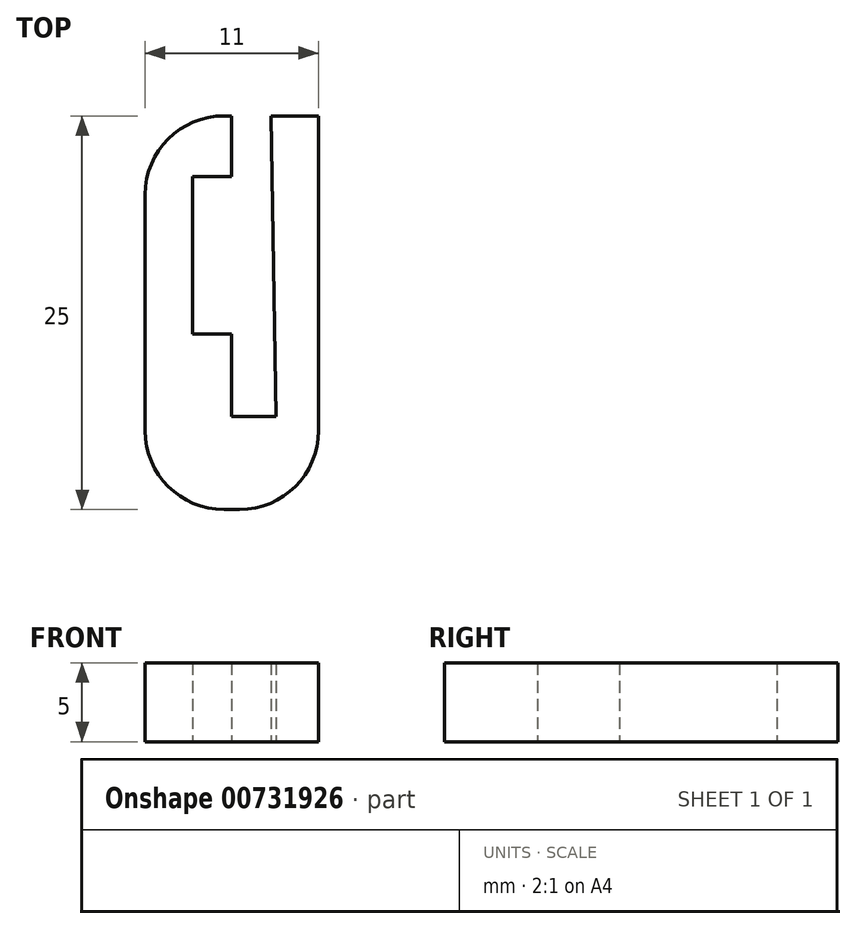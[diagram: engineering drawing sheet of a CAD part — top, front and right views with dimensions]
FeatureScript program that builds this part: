
annotation { "Feature Type Name" : "Feature", "Feature Type Description" : "" }
export const myFeature = defineFeature(function(context is Context, id is Id, definition is map)
    precondition{}
    {
        {
            var Q0;
            Q0=qCreatedBy(makeId("Top.planeOp"),FACE);
            var sketch = newSketch(context, id + "F0", { "sketchPlane" : qUnion([Q0])});
            skLineSegment(sketch, "E0", {"start": v(0, 0) * mm, "end": v(0, 25) * mm});
            skLineSegment(sketch, "E1", {"start": v(0, 25) * mm, "end": v(5.5, 25) * mm});
            skLineSegment(sketch, "E2", {"start": v(5.5, 25) * mm, "end": v(5.5, 21.13) * mm});
            skLineSegment(sketch, "E3", {"start": v(5.5, 5.92) * mm, "end": v(8.3, 5.92) * mm});
            skLineSegment(sketch, "E4", {"start": v(8.3, 5.92) * mm, "end": v(8, 25) * mm});
            skLineSegment(sketch, "E5", {"start": v(8, 25) * mm, "end": v(11, 25) * mm});
            skLineSegment(sketch, "E6", {"start": v(11, 25) * mm, "end": v(11, 0) * mm});
            skLineSegment(sketch, "E7", {"start": v(11, 0) * mm, "end": v(0, 0) * mm});
            skLineSegment(sketch, "E8.bottom", {"start": v(5.5, 21.13) * mm, "end": v(3, 21.13) * mm});
            skLineSegment(sketch, "E8.top", {"start": v(5.5, 11.13) * mm, "end": v(3, 11.13) * mm});
            skLineSegment(sketch, "E8.right", {"start": v(3, 21.13) * mm, "end": v(3, 11.13) * mm});
            skLineSegment(sketch, "E9.trimOffspring", {"start": v(5.5, 11.13) * mm, "end": v(5.5, 5.92) * mm});
            skSolve(sketch);
        }
        {
            var Q0;
            Q0 = qSketchRegion(id + "F0", true);
            extrude(context, id + "F1", {"entities" : qUnion([Q0]), "depth" : 5 * mm, "offsetDistance" : 25 * mm});
        }
        {
            var Q0;
            Q0=makeQuery(id+"F1.opExtrude","SWEPT_EDGE",EDGE,{"disambiguationData":[OSD([sQuery(id+"F0.wireOp",EDGE,"E0"),sQuery(id+"F0.wireOp",EDGE,"E1")])]});
            var Q1;
            Q1=makeQuery(id+"F1.opExtrude","SWEPT_EDGE",EDGE,{"disambiguationData":[OSD([sQuery(id+"F0.wireOp",EDGE,"E0"),sQuery(id+"F0.wireOp",EDGE,"E7")])]});
            var Q2;
            Q2=makeQuery(id+"F1.opExtrude","SWEPT_EDGE",EDGE,{"disambiguationData":[OSD([sQuery(id+"F0.wireOp",EDGE,"E6"),sQuery(id+"F0.wireOp",EDGE,"E7")])]});
            fillet(context, id + "F2", {"entities" : qUnion([Q0, Q1, Q2]), "radius" : 5 * mm, "tangentPropagation" : true, "allowEdgeOverflow" : false});
        }
    });
